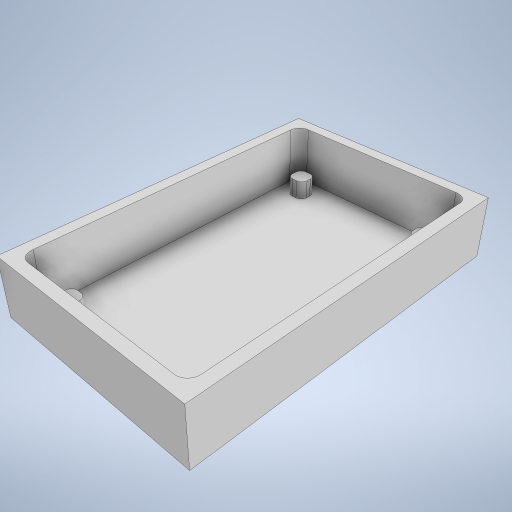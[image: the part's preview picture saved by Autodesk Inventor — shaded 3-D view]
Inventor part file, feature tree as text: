
AUTODESK INVENTOR PART (.ipt)
format: ipt  version: 2024 (Build 280153000, 153)  size: 308,736 bytes
history: native  units: mm
features: other x4, extrude x3, sketch x3, projected_geometry x2
ambient origin geometry x8: Origin, YZ Plane, XZ Plane, XY Plane, X Axis, Y Axis, Z Axis, Center Point
bodies: 实体1 (feature_tree)
feature tree (12):
  extrude  "拉伸1"  Depth=90.0mm
  extrude  "拉伸2"  Depth=80.0mm
  other  "面圆角1"
  other  "面圆角2"
  other  "面圆角3"
  other  "面圆角4"
  extrude  "拉伸3"  Depth=23.8mm TaperAngle=0.0deg
  sketch  "草图1"  dims[d0=140.0mm d1=90.0mm]
  sketch  "草图2"  dims[d2=25.0mm d3=0.0mm d4=80.0mm]
  projected_geometry  "投影回路1"
  sketch  "草图4"  dims[d5=130.0mm d6=23.8mm d7=0.0mm d8=5.0mm d9=5.0mm d10=5.0mm d11=5.0mm d12=55.88mm d13=29.848mm d14=8.0mm d15=8.0mm d16=3.0mm d17=59.696mm d18=111.76mm d19=20.0mm d21=59.696mm d22=20.0mm d24=111.76mm d27=8.0mm d28=0.0mm]
  projected_geometry  "投影回路2"
